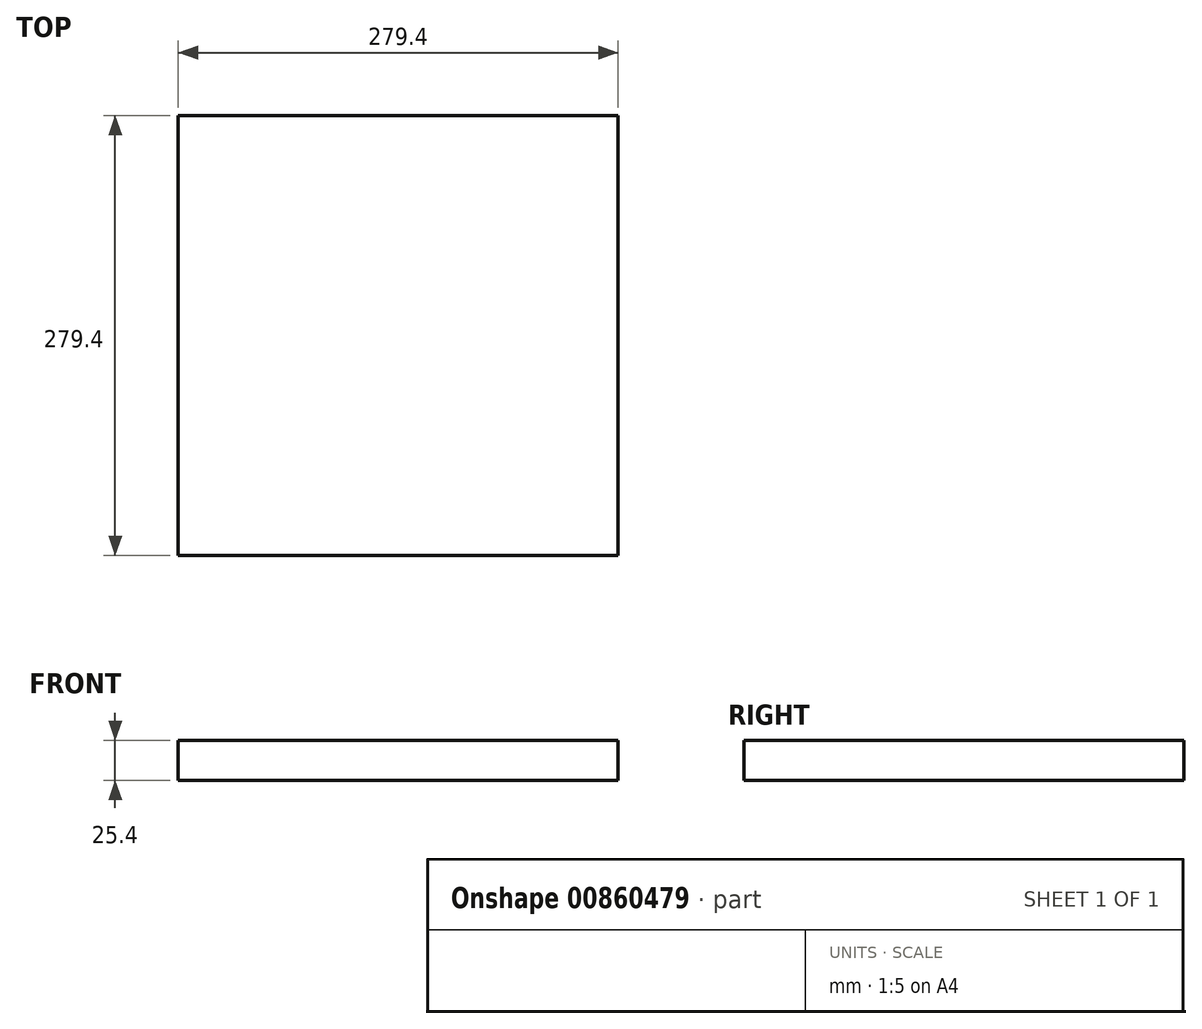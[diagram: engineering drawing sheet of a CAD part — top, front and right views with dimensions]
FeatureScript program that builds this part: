
annotation { "Feature Type Name" : "Feature", "Feature Type Description" : "" }
export const myFeature = defineFeature(function(context is Context, id is Id, definition is map)
    precondition{}
    {
        {
            var Q0;
            Q0=qCreatedBy(makeId("Top.planeOp"),FACE);
            var sketch = newSketch(context, id + "F0", { "sketchPlane" : qUnion([Q0])});
            skLineSegment(sketch, "E0.bottom", {"start": v(-139.7, -139.7) * mm, "end": v(139.7, -139.7) * mm});
            skLineSegment(sketch, "E0.top", {"start": v(-139.7, 139.7) * mm, "end": v(139.7, 139.7) * mm});
            skLineSegment(sketch, "E0.left", {"start": v(-139.7, -139.7) * mm, "end": v(-139.7, 139.7) * mm});
            skLineSegment(sketch, "E0.right", {"start": v(139.7, -139.7) * mm, "end": v(139.7, 139.7) * mm});
            skPoint(sketch, "E0.middle", {"position": v(0, 0) * mm});
            skSolve(sketch);
        }
        {
            var Q0;
            Q0=makeQuery(id+"F0.imprint","IMPRINT",FACE,{"disambiguationData":[TD([[makeQuery(id+"F0.imprint","IMPRINT",EDGE,{"derivedFrom":sQuery(id+"F0.wireOp",EDGE,"E0.bottom")}),1.0]])]});
            extrude(context, id + "F1", {"entities" : qUnion([Q0]), "depth" : 25.4 * mm, "offsetDistance" : 25.4 * mm});
        }
    });
